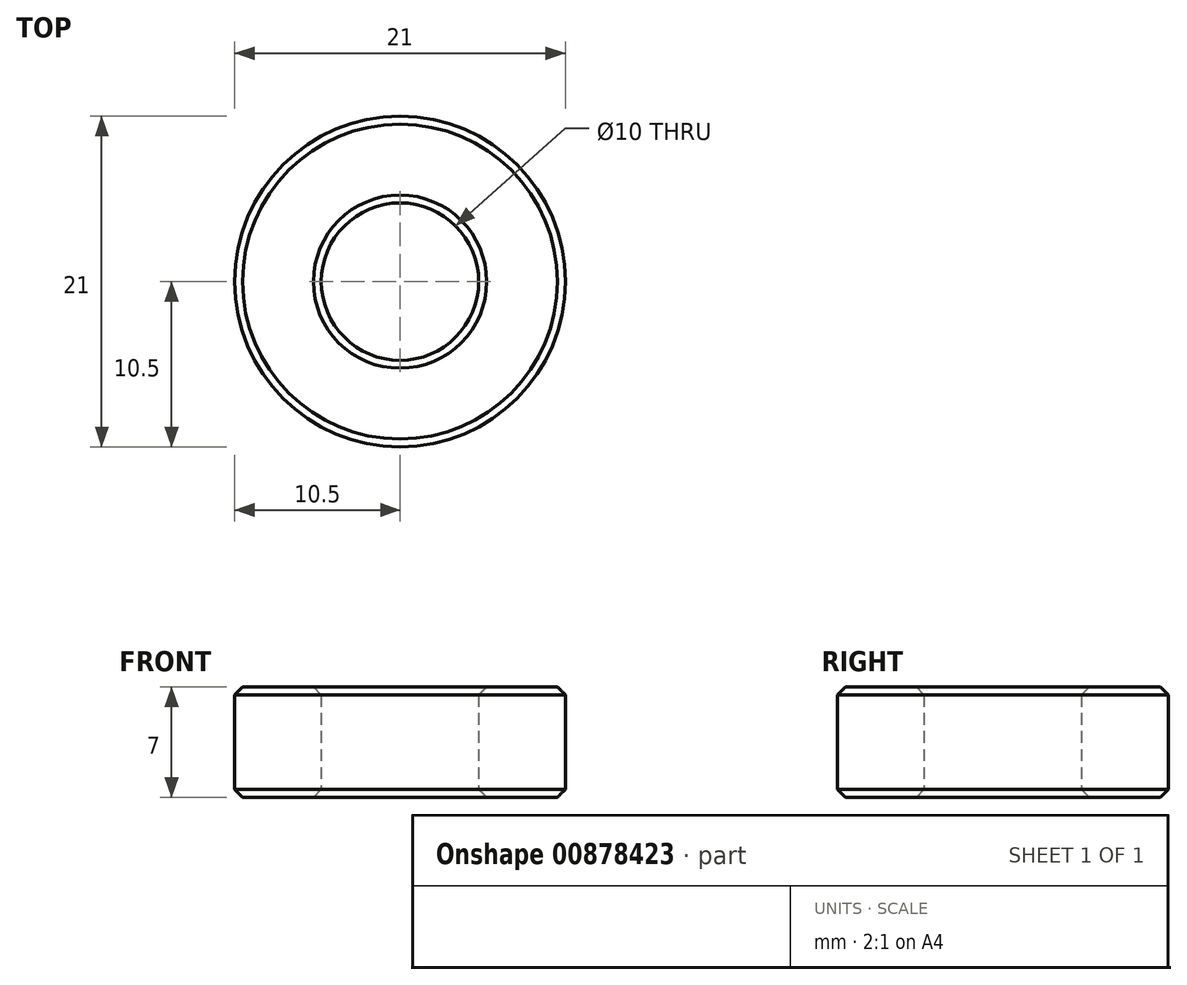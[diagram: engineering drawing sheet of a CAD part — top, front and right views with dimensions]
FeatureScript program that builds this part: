
annotation { "Feature Type Name" : "Feature", "Feature Type Description" : "" }
export const myFeature = defineFeature(function(context is Context, id is Id, definition is map)
    precondition{}
    {
        {
            var Q0;
            Q0=qCreatedBy(makeId("Front.planeOp"),FACE);
            var sketch = newSketch(context, id + "F0", { "sketchPlane" : qUnion([Q0])});
            skLineSegment(sketch, "E0", {"start": v(0, 0) * mm, "end": v(0, 37.54) * mm, "construction": true});
            skLineSegment(sketch, "E1.bottom", {"start": v(-10.5, 22) * mm, "end": v(-5, 22) * mm});
            skLineSegment(sketch, "E1.top", {"start": v(-10.5, 15) * mm, "end": v(-5, 15) * mm});
            skLineSegment(sketch, "E1.left", {"start": v(-10.5, 22) * mm, "end": v(-10.5, 15) * mm});
            skLineSegment(sketch, "E1.right", {"start": v(-5, 22) * mm, "end": v(-5, 15) * mm});
            skSolve(sketch);
        }
        {
            var Q0;
            Q0=makeQuery(id+"F0.imprint","IMPRINT",FACE,{"disambiguationData":[TD([[makeQuery(id+"F0.imprint","IMPRINT",EDGE,{"derivedFrom":sQuery(id+"F0.wireOp",EDGE,"E1.bottom")}),-1.0]])]});
            var Q1;
            Q1=sQuery(id+"F0.wireOp",EDGE,"E0");
            revolve(context, id + "F1", {"surfaceOperationType" : NewSurfaceOperationType.NEW, "entities" : qUnion([Q0]), "axis" : qUnion([Q1]), "revolveType" : RevolveType.FULL});
        }
        {
            var Q0;
            Q0=makeQuery(id+"F1.opRevolve","SWEPT_EDGE",EDGE,{"disambiguationData":[OSD([sQuery(id+"F0.wireOp",EDGE,"E1.bottom"),sQuery(id+"F0.wireOp",EDGE,"E1.left")])]});
            var Q1;
            Q1=makeQuery(id+"F1.opRevolve","SWEPT_EDGE",EDGE,{"disambiguationData":[OSD([sQuery(id+"F0.wireOp",EDGE,"E1.bottom"),sQuery(id+"F0.wireOp",EDGE,"E1.right")])]});
            var Q2;
            Q2=makeQuery(id+"F1.opRevolve","SWEPT_EDGE",EDGE,{"disambiguationData":[OSD([sQuery(id+"F0.wireOp",EDGE,"E1.top"),sQuery(id+"F0.wireOp",EDGE,"E1.left")])]});
            var Q3;
            Q3=makeQuery(id+"F1.opRevolve","SWEPT_EDGE",EDGE,{"disambiguationData":[OSD([sQuery(id+"F0.wireOp",EDGE,"E1.top"),sQuery(id+"F0.wireOp",EDGE,"E1.right")])]});
            chamfer(context, id + "F2", {"entities" : qUnion([Q0, Q1, Q2, Q3]), "width" : 0.5 * mm, "tangentPropagation" : true});
        }
    });
